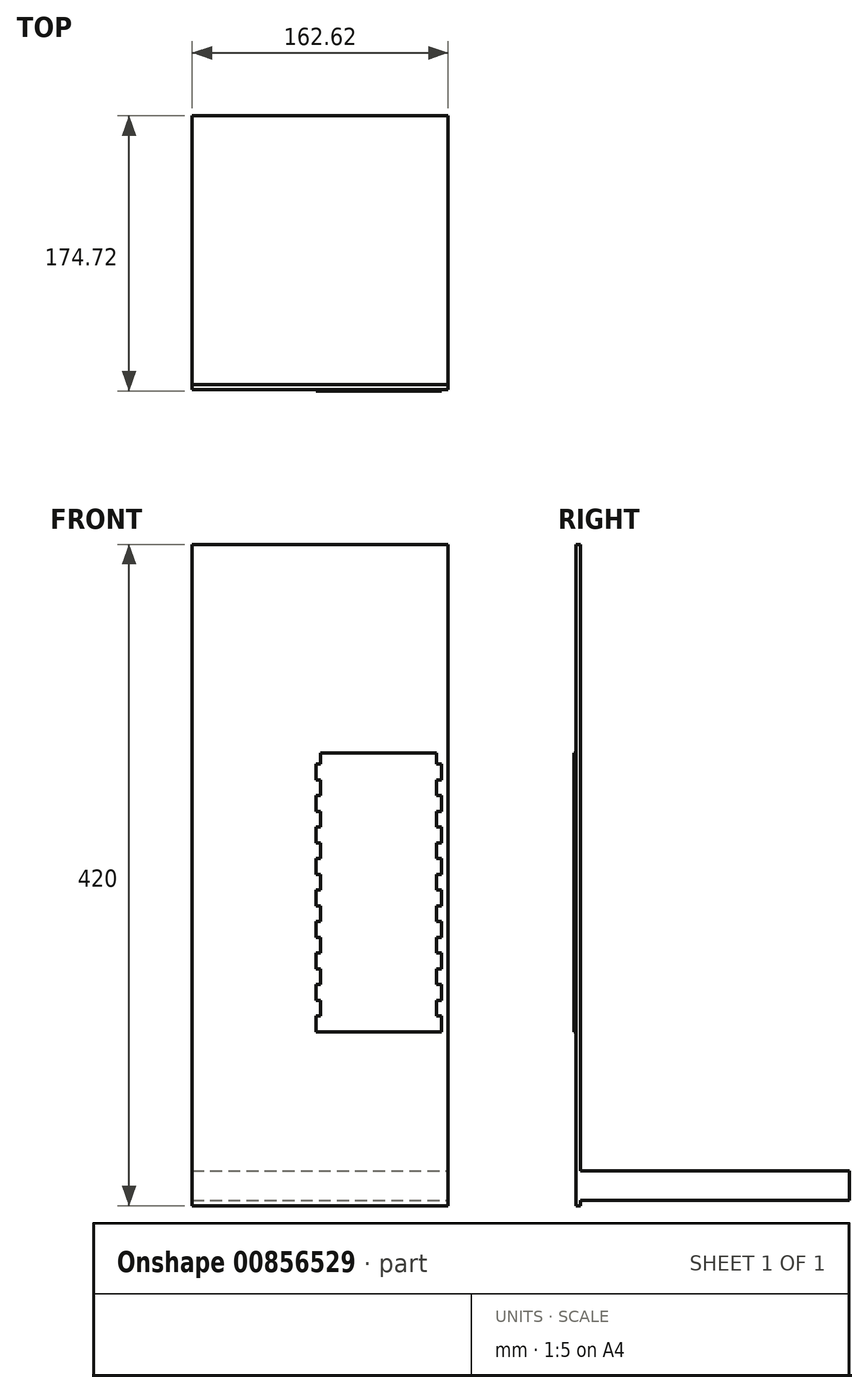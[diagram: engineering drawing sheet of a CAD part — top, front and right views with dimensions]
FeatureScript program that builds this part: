
annotation { "Feature Type Name" : "Feature", "Feature Type Description" : "" }
export const myFeature = defineFeature(function(context is Context, id is Id, definition is map)
    precondition{}
    {
        {
            var Q0;
            Q0=qCreatedBy(makeId("Front.planeOp"),FACE);
            var sketch = newSketch(context, id + "F0", { "sketchPlane" : qUnion([Q0])});
            skLineSegment(sketch, "E0.bottom", {"start": v(-118.45, 215.63) * mm, "end": v(44.17, 215.63) * mm});
            skLineSegment(sketch, "E0.top", {"start": v(-118.45, -204.37) * mm, "end": v(44.17, -204.37) * mm});
            skLineSegment(sketch, "E0.left", {"start": v(-118.45, 215.63) * mm, "end": v(-118.45, -204.37) * mm});
            skLineSegment(sketch, "E0.right", {"start": v(44.17, 215.63) * mm, "end": v(44.17, -204.37) * mm});
            skSolve(sketch);
        }
        {
            var Q0;
            Q0 = qSketchRegion(id + "F0", true);
            extrude(context, id + "F1", {"entities" : qUnion([Q0]), "depth" : 3 * mm, "offsetDistance" : 25 * mm});
        }
        {
            var Q0;
            Q0=qCreatedBy(makeId("Right.planeOp"),FACE);
            var sketch = newSketch(context, id + "F2", { "sketchPlane" : qUnion([Q0])});
            skLineSegment(sketch, "E1.bottom", {"start": v(0, -200.94) * mm, "end": v(170.72, -200.94) * mm});
            skLineSegment(sketch, "E1.top", {"start": v(0, -182.4) * mm, "end": v(170.72, -182.4) * mm});
            skLineSegment(sketch, "E1.left", {"start": v(0, -182.4) * mm, "end": v(0, -200.94) * mm});
            skLineSegment(sketch, "E1.right", {"start": v(170.72, -182.4) * mm, "end": v(170.72, -200.94) * mm});
            skSolve(sketch);
        }
        {
            var Q0;
            Q0=makeQuery(id+"F2.imprint","IMPRINT",FACE,{"disambiguationData":[TD([[makeQuery(id+"F2.imprint","IMPRINT",EDGE,{"derivedFrom":sQuery(id+"F2.wireOp",EDGE,"E1.bottom")}),1.0]])]});
            var Q1;
            Q1=makeQuery(id+"F1.opExtrude","SWEPT_FACE",FACE,{"disambiguationData":[OSD([sQuery(id+"F0.wireOp",EDGE,"E0.left")])]});
            extrude(context, id + "F3", {"entities" : qUnion([Q0]), "endBound" : BoundingType.UP_TO_SURFACE, "oppositeDirection" : true, "depth" : 25 * mm, "endBoundEntityFace" : qUnion([Q1]), "offsetDistance" : 25 * mm});
        }
        {
            var Q0;
            Q0=makeQuery(id+"F3.opExtrude","CAP_FACE",FACE,{"disambiguationData":[OSD([sQuery(id+"F2.wireOp",EDGE,"E1.bottom"),sQuery(id+"F2.wireOp",EDGE,"E1.top"),sQuery(id+"F2.wireOp",EDGE,"E1.left"),sQuery(id+"F2.wireOp",EDGE,"E1.right")])],"isStart":true});
            var Q1;
            Q1=makeQuery(id+"F1.opExtrude","SWEPT_FACE",FACE,{"disambiguationData":[OSD([sQuery(id+"F0.wireOp",EDGE,"E0.right")])]});
            extrude(context, id + "F4", {"entities" : qUnion([Q0]), "operationType" : NewBodyOperationType.ADD, "endBound" : BoundingType.UP_TO_SURFACE, "depth" : 25 * mm, "endBoundEntityFace" : qUnion([Q1]), "offsetDistance" : 25 * mm});
        }
        {
            var Q0;
            Q0=qCreatedBy(makeId("Front.planeOp"),FACE);
            var sketch = newSketch(context, id + "F5", { "sketchPlane" : qUnion([Q0])});
            skLineSegment(sketch, "E2", {"start": v(-39.79, -93.85) * mm, "end": v(-39.79, -83.85) * mm});
            skLineSegment(sketch, "E3", {"start": v(-39.79, -83.85) * mm, "end": v(-36.79, -83.85) * mm});
            skLineSegment(sketch, "E4", {"start": v(-36.79, -83.85) * mm, "end": v(-36.79, -73.85) * mm});
            skLineSegment(sketch, "E5", {"start": v(-36.79, -73.85) * mm, "end": v(-39.79, -73.85) * mm});
            skLineSegment(sketch, "E6.1.0.0", {"start": v(-39.79, -63.85) * mm, "end": v(-36.79, -63.85) * mm});
            skLineSegment(sketch, "E6.1.0.1", {"start": v(-36.79, -63.85) * mm, "end": v(-36.79, -53.85) * mm});
            skLineSegment(sketch, "E6.1.0.2", {"start": v(-36.79, -53.85) * mm, "end": v(-39.79, -53.85) * mm});
            skLineSegment(sketch, "E6.1.0.3", {"start": v(-39.79, -73.85) * mm, "end": v(-39.79, -63.85) * mm});
            skLineSegment(sketch, "E6.2.0.0", {"start": v(-39.79, -43.85) * mm, "end": v(-36.79, -43.85) * mm});
            skLineSegment(sketch, "E6.2.0.1", {"start": v(-36.79, -43.85) * mm, "end": v(-36.79, -33.85) * mm});
            skLineSegment(sketch, "E6.2.0.2", {"start": v(-36.79, -33.85) * mm, "end": v(-39.79, -33.85) * mm});
            skLineSegment(sketch, "E6.2.0.3", {"start": v(-39.79, -53.85) * mm, "end": v(-39.79, -43.85) * mm});
            skLineSegment(sketch, "E6.3.0.0", {"start": v(-39.79, -23.85) * mm, "end": v(-36.79, -23.85) * mm});
            skLineSegment(sketch, "E6.3.0.1", {"start": v(-36.79, -23.85) * mm, "end": v(-36.79, -13.85) * mm});
            skLineSegment(sketch, "E6.3.0.2", {"start": v(-36.79, -13.85) * mm, "end": v(-39.79, -13.85) * mm});
            skLineSegment(sketch, "E6.3.0.3", {"start": v(-39.79, -33.85) * mm, "end": v(-39.79, -23.85) * mm});
            skLineSegment(sketch, "E6.4.0.0", {"start": v(-39.79, -3.85) * mm, "end": v(-36.79, -3.85) * mm});
            skLineSegment(sketch, "E6.4.0.1", {"start": v(-36.79, -3.85) * mm, "end": v(-36.79, 6.15) * mm});
            skLineSegment(sketch, "E6.4.0.2", {"start": v(-36.79, 6.15) * mm, "end": v(-39.79, 6.15) * mm});
            skLineSegment(sketch, "E6.4.0.3", {"start": v(-39.79, -13.85) * mm, "end": v(-39.79, -3.85) * mm});
            skLineSegment(sketch, "E6.5.0.0", {"start": v(-39.79, 16.15) * mm, "end": v(-36.79, 16.15) * mm});
            skLineSegment(sketch, "E6.5.0.1", {"start": v(-36.79, 16.15) * mm, "end": v(-36.79, 26.15) * mm});
            skLineSegment(sketch, "E6.5.0.2", {"start": v(-36.79, 26.15) * mm, "end": v(-39.79, 26.15) * mm});
            skLineSegment(sketch, "E6.5.0.3", {"start": v(-39.79, 6.15) * mm, "end": v(-39.79, 16.15) * mm});
            skLineSegment(sketch, "E6.6.0.0", {"start": v(-39.79, 36.15) * mm, "end": v(-36.79, 36.15) * mm});
            skLineSegment(sketch, "E6.6.0.1", {"start": v(-36.79, 36.15) * mm, "end": v(-36.79, 46.15) * mm});
            skLineSegment(sketch, "E6.6.0.2", {"start": v(-36.79, 46.15) * mm, "end": v(-39.79, 46.15) * mm});
            skLineSegment(sketch, "E6.6.0.3", {"start": v(-39.79, 26.15) * mm, "end": v(-39.79, 36.15) * mm});
            skLineSegment(sketch, "E6.7.0.0", {"start": v(-39.79, 56.15) * mm, "end": v(-36.79, 56.15) * mm});
            skLineSegment(sketch, "E6.7.0.1", {"start": v(-36.79, 56.15) * mm, "end": v(-36.79, 66.15) * mm});
            skLineSegment(sketch, "E6.7.0.2", {"start": v(-36.79, 66.15) * mm, "end": v(-39.79, 66.15) * mm});
            skLineSegment(sketch, "E6.7.0.3", {"start": v(-39.79, 46.15) * mm, "end": v(-39.79, 56.15) * mm});
            skLineSegment(sketch, "E6.8.0.0", {"start": v(-39.79, 76.15) * mm, "end": v(-36.79, 76.15) * mm});
            skLineSegment(sketch, "E6.8.0.1", {"start": v(-36.79, 76.15) * mm, "end": v(-36.79, 83.1) * mm});
            skLineSegment(sketch, "E6.8.0.3", {"start": v(-39.79, 66.15) * mm, "end": v(-39.79, 76.15) * mm});
            skLineSegment(sketch, "E7", {"start": v(0, 0) * mm, "end": v(0, 75.15) * mm, "construction": true});
            skLineSegment(sketch, "E8", {"start": v(0, 0) * mm, "end": v(0, -74.64) * mm, "construction": true});
            skLineSegment(sketch, "E9.MirrorCS", {"start": v(39.79, -63.85) * mm, "end": v(36.79, -63.85) * mm});
            skLineSegment(sketch, "E10.MirrorCS", {"start": v(36.79, -33.85) * mm, "end": v(39.79, -33.85) * mm});
            skLineSegment(sketch, "E11.MirrorCS", {"start": v(36.79, -73.85) * mm, "end": v(39.79, -73.85) * mm});
            skLineSegment(sketch, "E12.MirrorCS", {"start": v(36.79, -13.85) * mm, "end": v(39.79, -13.85) * mm});
            skLineSegment(sketch, "E13.MirrorCS", {"start": v(39.79, 16.15) * mm, "end": v(36.79, 16.15) * mm});
            skLineSegment(sketch, "E14.MirrorCS", {"start": v(36.79, -53.85) * mm, "end": v(39.79, -53.85) * mm});
            skLineSegment(sketch, "E15.MirrorCS", {"start": v(36.79, 46.15) * mm, "end": v(39.79, 46.15) * mm});
            skLineSegment(sketch, "E16.MirrorCS", {"start": v(39.79, 56.15) * mm, "end": v(36.79, 56.15) * mm});
            skLineSegment(sketch, "E17.MirrorCS", {"start": v(39.79, -43.85) * mm, "end": v(36.79, -43.85) * mm});
            skLineSegment(sketch, "E18.MirrorCS", {"start": v(39.79, 76.15) * mm, "end": v(36.79, 76.15) * mm});
            skLineSegment(sketch, "E19.MirrorCS", {"start": v(36.79, 6.15) * mm, "end": v(39.79, 6.15) * mm});
            skLineSegment(sketch, "E20.MirrorCS", {"start": v(36.79, 66.15) * mm, "end": v(39.79, 66.15) * mm});
            skLineSegment(sketch, "E21.MirrorCS", {"start": v(36.79, 26.15) * mm, "end": v(39.79, 26.15) * mm});
            skLineSegment(sketch, "E22.MirrorCS", {"start": v(39.79, -23.85) * mm, "end": v(36.79, -23.85) * mm});
            skLineSegment(sketch, "E23.MirrorCS", {"start": v(39.79, -3.85) * mm, "end": v(36.79, -3.85) * mm});
            skLineSegment(sketch, "E24.MirrorCS", {"start": v(39.79, 36.15) * mm, "end": v(36.79, 36.15) * mm});
            skLineSegment(sketch, "E25.MirrorCS", {"start": v(39.79, -83.85) * mm, "end": v(36.79, -83.85) * mm});
            skLineSegment(sketch, "E26.MirrorCS", {"start": v(39.79, -73.85) * mm, "end": v(39.79, -63.85) * mm});
            skLineSegment(sketch, "E27.MirrorCS", {"start": v(39.79, 66.15) * mm, "end": v(39.79, 76.15) * mm});
            skLineSegment(sketch, "E28.MirrorCS", {"start": v(39.79, -93.85) * mm, "end": v(39.79, -83.85) * mm});
            skLineSegment(sketch, "E29.MirrorCS", {"start": v(36.79, 76.15) * mm, "end": v(36.79, 83.1) * mm});
            skLineSegment(sketch, "E30.MirrorCS", {"start": v(36.79, -83.85) * mm, "end": v(36.79, -73.85) * mm});
            skLineSegment(sketch, "E31.MirrorCS", {"start": v(39.79, 26.15) * mm, "end": v(39.79, 36.15) * mm});
            skLineSegment(sketch, "E32.MirrorCS", {"start": v(39.79, -53.85) * mm, "end": v(39.79, -43.85) * mm});
            skLineSegment(sketch, "E33.MirrorCS", {"start": v(36.79, -43.85) * mm, "end": v(36.79, -33.85) * mm});
            skLineSegment(sketch, "E34.MirrorCS", {"start": v(39.79, -13.85) * mm, "end": v(39.79, -3.85) * mm});
            skLineSegment(sketch, "E35.MirrorCS", {"start": v(36.79, -23.85) * mm, "end": v(36.79, -13.85) * mm});
            skLineSegment(sketch, "E36.MirrorCS", {"start": v(36.79, -63.85) * mm, "end": v(36.79, -53.85) * mm});
            skLineSegment(sketch, "E37.MirrorCS", {"start": v(36.79, 36.15) * mm, "end": v(36.79, 46.15) * mm});
            skLineSegment(sketch, "E38.MirrorCS", {"start": v(39.79, -33.85) * mm, "end": v(39.79, -23.85) * mm});
            skLineSegment(sketch, "E39.MirrorCS", {"start": v(39.79, 6.15) * mm, "end": v(39.79, 16.15) * mm});
            skLineSegment(sketch, "E40.MirrorCS", {"start": v(39.79, 46.15) * mm, "end": v(39.79, 56.15) * mm});
            skLineSegment(sketch, "E41.MirrorCS", {"start": v(36.79, 16.15) * mm, "end": v(36.79, 26.15) * mm});
            skLineSegment(sketch, "E42.MirrorCS", {"start": v(36.79, -3.85) * mm, "end": v(36.79, 6.15) * mm});
            skLineSegment(sketch, "E43.MirrorCS", {"start": v(36.79, 56.15) * mm, "end": v(36.79, 66.15) * mm});
            skLineSegment(sketch, "E44", {"start": v(-39.79, -93.85) * mm, "end": v(39.79, -93.85) * mm});
            skLineSegment(sketch, "E45", {"start": v(-36.79, 83.1) * mm, "end": v(36.79, 83.1) * mm});
            skSolve(sketch);
        }
        {
            var Q0;
            Q0 = qSketchRegion(id + "F5", true);
            extrude(context, id + "F6", {"entities" : qUnion([Q0]), "depth" : 4 * mm, "offsetDistance" : 25 * mm});
        }
        {
            var Q0;
            Q0 = qSketchRegion(id + "F5", true);
            extrude(context, id + "F7", {"entities" : qUnion([Q0]), "operationType" : NewBodyOperationType.ADD, "depth" : 4 * mm, "offsetDistance" : 25 * mm});
        }
    });
